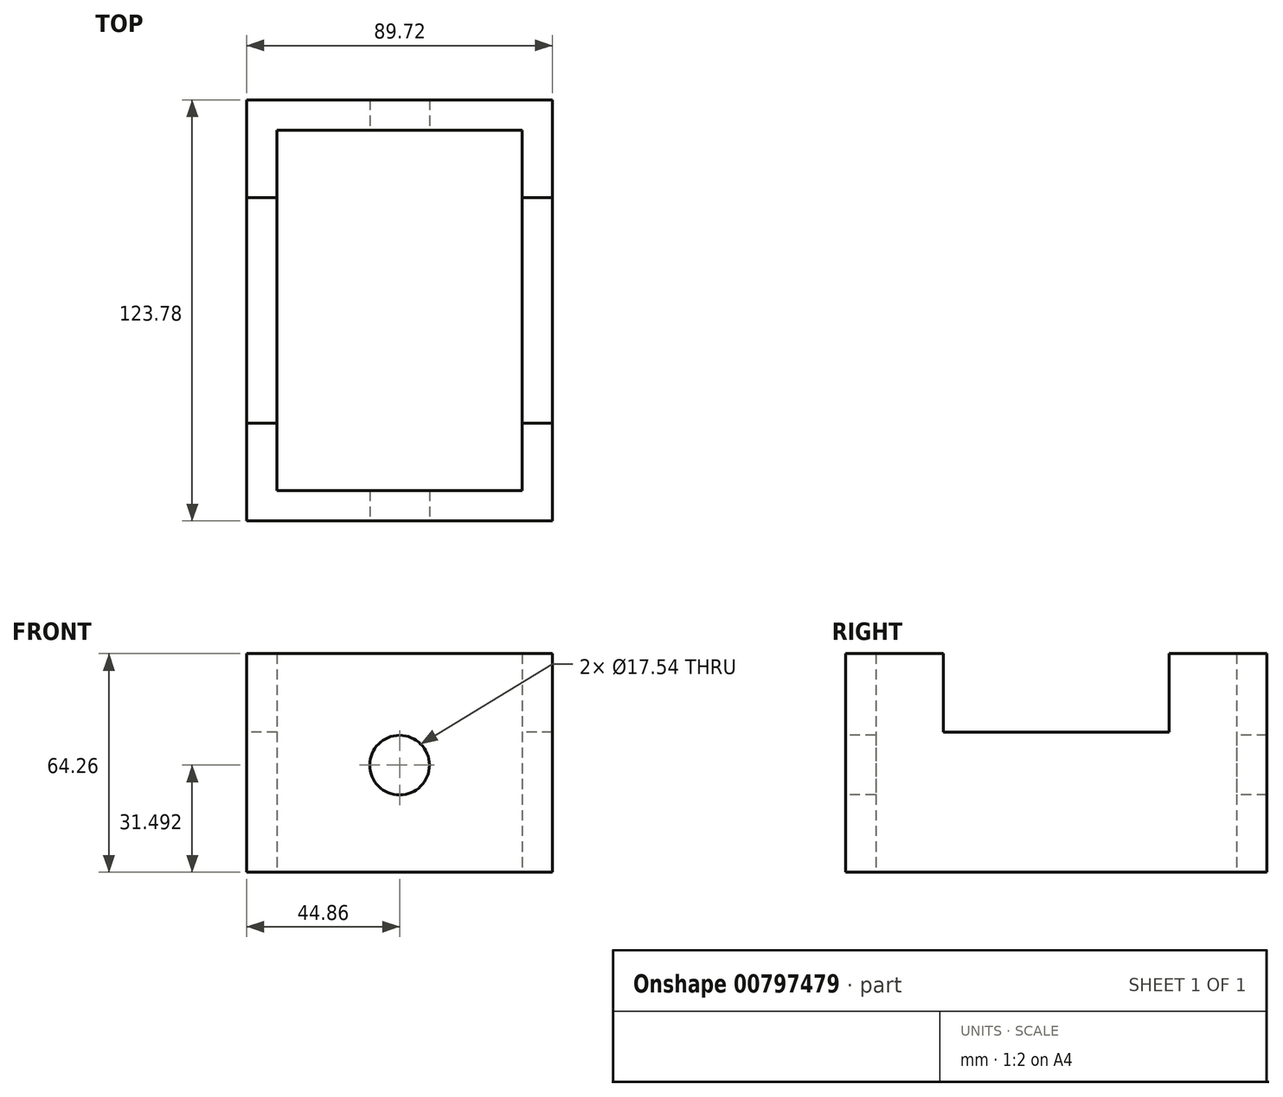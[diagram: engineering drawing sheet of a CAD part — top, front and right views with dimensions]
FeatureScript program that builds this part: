
annotation { "Feature Type Name" : "Feature", "Feature Type Description" : "" }
export const myFeature = defineFeature(function(context is Context, id is Id, definition is map)
    precondition{}
    {
        {
            var Q0;
            Q0=qCreatedBy(makeId("Top.planeOp"),FACE);
            var sketch = newSketch(context, id + "F0", { "sketchPlane" : qUnion([Q0])});
            skLineSegment(sketch, "E0.bottom", {"start": v(-35.97, 53) * mm, "end": v(35.97, 53) * mm});
            skLineSegment(sketch, "E0.top", {"start": v(-35.97, -53) * mm, "end": v(35.97, -53) * mm});
            skLineSegment(sketch, "E0.left", {"start": v(-35.97, 53) * mm, "end": v(-35.97, -53) * mm});
            skLineSegment(sketch, "E0.right", {"start": v(35.97, 53) * mm, "end": v(35.97, -53) * mm});
            skPoint(sketch, "E0.middle", {"position": v(0, 0) * mm});
            skLineSegment(sketch, "E1.0", {"start": v(-44.86, 61.89) * mm, "end": v(44.86, 61.89) * mm});
            skLineSegment(sketch, "E1.1", {"start": v(-44.86, 61.89) * mm, "end": v(-44.86, -61.89) * mm});
            skLineSegment(sketch, "E1.2", {"start": v(-44.86, -61.89) * mm, "end": v(44.86, -61.89) * mm});
            skLineSegment(sketch, "E1.3", {"start": v(44.86, 61.89) * mm, "end": v(44.86, -61.89) * mm});
            skSolve(sketch);
        }
        {
            var Q0;
            Q0=makeQuery(id+"F0.imprint","IMPRINT",FACE,{"disambiguationData":[TD([[makeQuery(id+"F0.imprint","IMPRINT",EDGE,{"derivedFrom":sQuery(id+"F0.wireOp",EDGE,"E0.bottom")}),1.0]])]});
            extrude(context, id + "F1", {"entities" : qUnion([Q0]), "depth" : 64.26 * mm, "offsetDistance" : 25.4 * mm});
        }
        {
            var Q0;
            Q0=makeQuery(id+"F1.opExtrude","SWEPT_FACE",FACE,{"disambiguationData":[OSD([sQuery(id+"F0.wireOp",EDGE,"E1.2")])]});
            var sketch = newSketch(context, id + "F2", { "sketchPlane" : qUnion([Q0])});
            skCircle(sketch, "E2", {"center": v(0, 31.5) * mm, "radius": 8.77 * mm});
            skSolve(sketch);
        }
        {
            var Q0;
            Q0 = qSketchRegion(id + "F2", true);
            extrude(context, id + "F3", {"entities" : qUnion([Q0]), "operationType" : NewBodyOperationType.REMOVE, "oppositeDirection" : true, "depth" : 149.86 * mm, "offsetDistance" : 25.4 * mm});
        }
        {
            var Q0;
            Q0=makeQuery(id+"F1.opExtrude","SWEPT_FACE",FACE,{"disambiguationData":[OSD([sQuery(id+"F0.wireOp",EDGE,"E1.1")])]});
            var sketch = newSketch(context, id + "F4", { "sketchPlane" : qUnion([Q0])});
            skLineSegment(sketch, "E3.bottom", {"start": v(-33.16, 41.22) * mm, "end": v(33.16, 41.22) * mm});
            skLineSegment(sketch, "E3.top", {"start": v(-33.16, 87.3) * mm, "end": v(33.16, 87.3) * mm});
            skLineSegment(sketch, "E3.left", {"start": v(-33.16, 41.22) * mm, "end": v(-33.16, 87.3) * mm});
            skLineSegment(sketch, "E3.right", {"start": v(33.16, 41.22) * mm, "end": v(33.16, 87.3) * mm});
            skPoint(sketch, "E3.middle", {"position": v(0, 64.26) * mm});
            skSolve(sketch);
        }
        {
            var Q0;
            Q0 = qSketchRegion(id + "F4", true);
            extrude(context, id + "F5", {"entities" : qUnion([Q0]), "operationType" : NewBodyOperationType.REMOVE, "oppositeDirection" : true, "depth" : 136.9 * mm, "offsetDistance" : 25.4 * mm});
        }
    });
